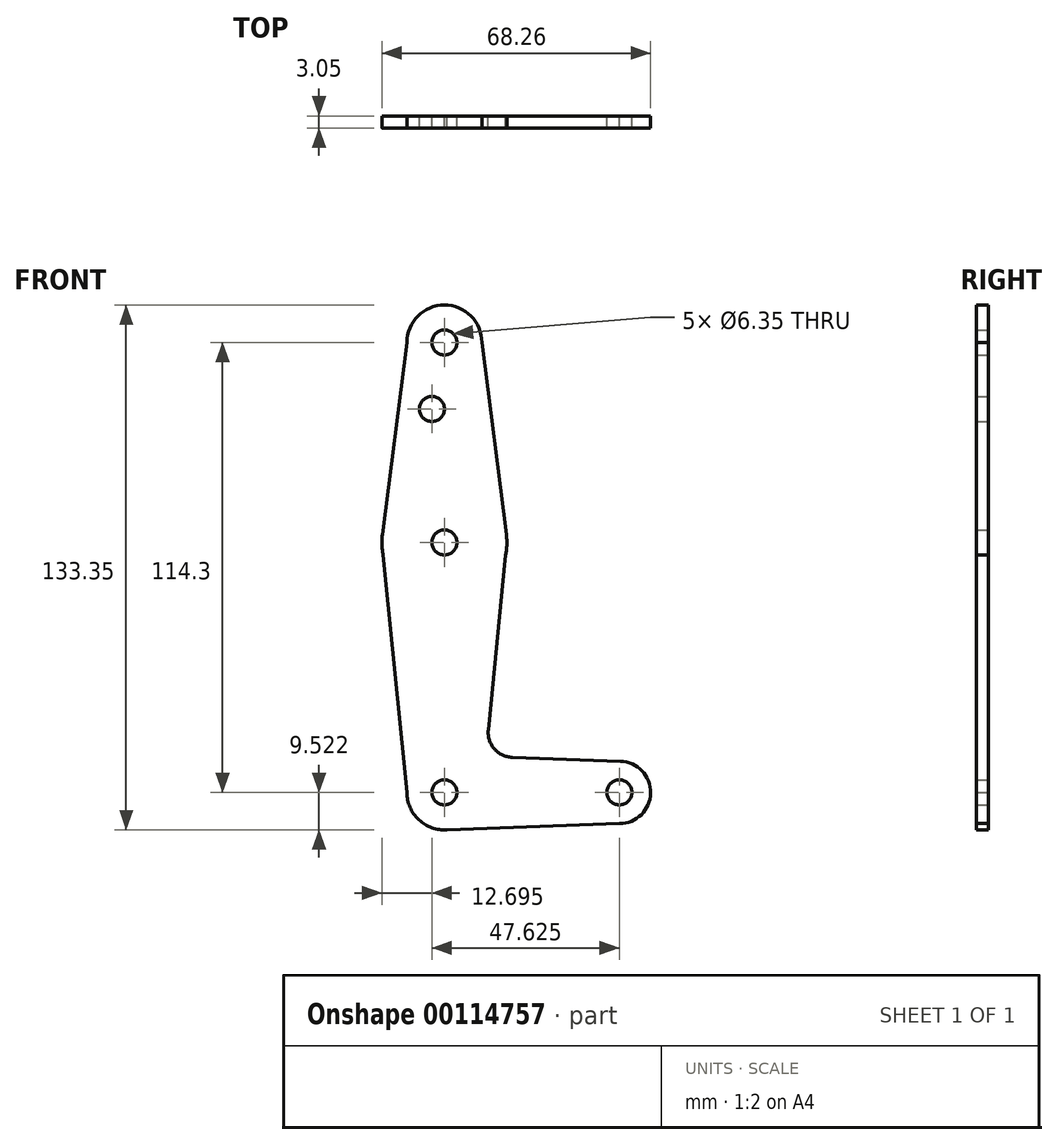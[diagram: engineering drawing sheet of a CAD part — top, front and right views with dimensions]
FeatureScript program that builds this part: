
annotation { "Feature Type Name" : "Feature", "Feature Type Description" : "" }
export const myFeature = defineFeature(function(context is Context, id is Id, definition is map)
    precondition{}
    {
        {
            var Q0;
            Q0=qCreatedBy(makeId("Front.planeOp"),FACE);
            var sketch = newSketch(context, id + "F0", { "sketchPlane" : qUnion([Q0])});
            skCircle(sketch, "E0", {"center": v(0, 101.87) * mm, "radius": 9.53 * mm});
            skCircle(sketch, "E1", {"center": v(0, 51.07) * mm, "radius": 15.88 * mm});
            skCircle(sketch, "E2", {"center": v(0, -12.43) * mm, "radius": 9.53 * mm});
            skLineSegment(sketch, "E3", {"start": v(0, 101.87) * mm, "end": v(0, 51.07) * mm, "construction": true});
            skLineSegment(sketch, "E4", {"start": v(0, 51.07) * mm, "end": v(0, -12.43) * mm, "construction": true});
            skLineSegment(sketch, "E5", {"start": v(0, -12.43) * mm, "end": v(44.45, -12.43) * mm, "construction": true});
            skCircle(sketch, "E6", {"center": v(44.45, -12.43) * mm, "radius": 7.94 * mm});
            skLineSegment(sketch, "E7", {"start": v(15.88, 51.07) * mm, "end": v(11.15, 3.46) * mm});
            skLineSegment(sketch, "E8", {"start": v(-15.88, 51.07) * mm, "end": v(-9.53, -12.43) * mm});
            skLineSegment(sketch, "E9", {"start": v(0, -21.95) * mm, "end": v(44.45, -20.37) * mm});
            skLineSegment(sketch, "E10", {"start": v(17.24, -3.52) * mm, "end": v(44.73, -4.5) * mm});
            skCircle(sketch, "E11", {"center": v(-3.17, 85) * mm, "radius": 3.18 * mm});
            skCircle(sketch, "E12", {"center": v(0, 51.07) * mm, "radius": 3.18 * mm});
            skCircle(sketch, "E13", {"center": v(0, -12.43) * mm, "radius": 3.18 * mm});
            skCircle(sketch, "E14", {"center": v(44.45, -12.43) * mm, "radius": 3.18 * mm});
            skCircle(sketch, "E15", {"center": v(0, 101.87) * mm, "radius": 3.18 * mm});
            skLineSegment(sketch, "E16", {"start": v(9.52, 101.87) * mm, "end": v(15.75, 53.08) * mm});
            skLineSegment(sketch, "E17", {"start": v(-9.53, 101.87) * mm, "end": v(-15.75, 53.08) * mm});
            skCircle(sketch, "E18", {"center": v(0, -12.43) * mm, "radius": 1.28 * mm});
            skPoint(sketch, "E19.newPointB", {"position": v(0, -2.9) * mm});
            skArc(sketch, "E19.filletArc", {"start": v(11.15, 3.46) * mm, "mid": v(12.69, -1.35) * mm, "end": v(17.24, -3.52) * mm});
            skSolve(sketch);
        }
        {
            var Q0;
            Q0 = qSketchRegion(id + "F0", true);
            extrude(context, id + "F1", {"entities" : qUnion([Q0]), "depth" : 3.05 * mm});
        }
    });
